# Revit family: D9515-DN25-RFA_2018
name_source: partatom
category: Pipe Accessories
revit_build: Autodesk Revit LT 2018 (Build: 20180329_1100(x64)
units: mm (PartAtom-declared; Revit-internal decimal feet)

## family parameters
Always vertical = Yes
Cut with Voids When Loaded = No
Part Type = Valve - Breaks Into
Round Connector Dimension = Use Diameter
Shared = No
Work Plane-Based = No

## types (6) — shared parameters
CAT0 = Yes
Description = Ruční vyvažovací ventil s měřením na cloně; PN25
H11 = 32 mm  [stored 0.104987 ft]
H13 = 9 mm  [stored 0.0295276 ft]
H15 = 20 mm  [stored 0.0656168 ft]
HWR = 35 mm  [stored 0.114829 ft]
L21 = 8 mm  [stored 0.0262467 ft]
L22 = 21 mm  [stored 0.0688976 ft]
L2D = 88 mm
L2D_Min = 3048 mm
L4 = 21 mm  [stored 0.0688976 ft]
L4__ve = -21 mm  [stored -0.0688976 ft]
L5 = 2 mm  [stored 0.00656168 ft]
Manufacturer = Hydronix
NUT1 = No
QmdConnectorList = 301;D;302;D
R14 = 20 mm  [stored 0.0656168 ft]
R6 = 8 mm  [stored 0.0262467 ft]
R7 = 9 mm  [stored 0.0295276 ft]
Type Comments = Ruční vyvažovací ventil s měřením na cloně; PN25; -10~+130°C; (měřicí vsuvky -10~+120°C)
URL = www.hydronix.cz
W2D = 15 mm  [stored 0.0492126 ft]
magiPartTypeId = 304
magiProductFamilyId = 2231140663314cd0b01ba8939d6b11

## per-type parameters (varying)
- D9515 DN15: CenSd_RN2_6=15 mm  [stored 0.0492126 ft]; CenSd_RN_6=15 mm  [stored 0.0492126 ft]; D=15 mm; H10=4 mm  [stored 0.0131234 ft]; H12=10 mm  [stored 0.0328084 ft]; H14=19 mm; H21=7 mm  [stored 0.0229659 ft]; H22=7 mm  [stored 0.0229659 ft]; H23=12 mm  [stored 0.0393701 ft]; H24=31 mm; L1=8 mm  [stored 0.0262467 ft]; L1__ve=-8 mm  [stored -0.0262467 ft]; L2=12 mm  [stored 0.0393701 ft]; L2__ve=-12 mm  [stored -0.0393701 ft]; L3=10 mm  [stored 0.0328084 ft]; L_2=44 mm; MC Product Code=9515 015 (DN15, PN25; kvs1,92; kvc2,80); R1=11 mm; R11=15 mm  [stored 0.0492126 ft]; R12=16 mm  [stored 0.0524934 ft]; R13=15 mm  [stored 0.0492126 ft]; R2=14 mm  [stored 0.0459318 ft]; R3=15 mm  [stored 0.0492126 ft]; RN=18 mm  [stored 0.0590551 ft]; RN2=18 mm  [stored 0.0590551 ft]; W21=7 mm  [stored 0.0229659 ft]; magiProductId=17cbc467cde14417a5a74aa240a316
- D9515 DN20: CenSd_RN2_6=17 mm  [stored 0.0557743 ft]; CenSd_RN_6=17 mm  [stored 0.0557743 ft]; D=20 mm; H10=5 mm  [stored 0.0164042 ft]; H12=10 mm  [stored 0.0328084 ft]; H14=18 mm  [stored 0.0590551 ft]; H21=8 mm  [stored 0.0262467 ft]; H22=8 mm  [stored 0.0262467 ft]; H23=12 mm  [stored 0.0393701 ft]; H24=31 mm; L1=9 mm  [stored 0.0295276 ft]; L1__ve=-9 mm  [stored -0.0295276 ft]; L2=12 mm  [stored 0.0393701 ft]; L2__ve=-12 mm  [stored -0.0393701 ft]; L3=10 mm  [stored 0.0328084 ft]; L_2=48 mm; MC Product Code=9515 020 (DN20, PN25; kvs3,67; kvc5,33); R1=13 mm  [stored 0.0426509 ft]; R11=16 mm  [stored 0.0524934 ft]; R12=18 mm  [stored 0.0590551 ft]; R13=16 mm  [stored 0.0524934 ft]; R2=15 mm  [stored 0.0492126 ft]; R3=16 mm  [stored 0.0524934 ft]; RN=20 mm  [stored 0.0656168 ft]; RN2=20 mm  [stored 0.0656168 ft]; W21=8 mm  [stored 0.0262467 ft]; magiProductId=db511cd39f454f418d6e49e6ac0c56
- D9515 DN25: CenSd_RN2_6=19 mm; CenSd_RN_6=19 mm; D=25 mm; H10=6 mm  [stored 0.019685 ft]; H12=10 mm  [stored 0.0328084 ft]; H14=17 mm  [stored 0.0557743 ft]; H21=10 mm  [stored 0.0328084 ft]; H22=10 mm  [stored 0.0328084 ft]; H23=12 mm  [stored 0.0393701 ft]; H24=31 mm; L1=10 mm  [stored 0.0328084 ft]; L1__ve=-10 mm  [stored -0.0328084 ft]; L2=14 mm  [stored 0.0459318 ft]; L2__ve=-14 mm  [stored -0.0459318 ft]; L3=12 mm  [stored 0.0393701 ft]; L_2=50 mm; MC Product Code=9515 025 (DN25, PN25; kvs6,24; kvc9,72); R1=14 mm  [stored 0.0459318 ft]; R11=18 mm  [stored 0.0590551 ft]; R12=20 mm  [stored 0.0656168 ft]; R13=18 mm  [stored 0.0590551 ft]; R2=17 mm  [stored 0.0557743 ft]; R3=18 mm  [stored 0.0590551 ft]; RN=21 mm  [stored 0.0688976 ft]; RN2=21 mm  [stored 0.0688976 ft]; W21=8 mm  [stored 0.0262467 ft]; magiProductId=e8aaae3d88cc438088acb51c2ae749
- D9515 DN32: CenSd_RN2_6=18 mm  [stored 0.0590551 ft]; CenSd_RN_6=21 mm  [stored 0.0688976 ft]; D=32 mm; H10=7 mm  [stored 0.0229659 ft]; H12=15 mm  [stored 0.0492126 ft]; H14=37 mm; H21=12 mm  [stored 0.0393701 ft]; H22=12 mm  [stored 0.0393701 ft]; H23=15 mm  [stored 0.0492126 ft]; H24=37 mm; L1=11 mm; L1__ve=-11 mm; L2=15 mm  [stored 0.0492126 ft]; L2__ve=-15 mm  [stored -0.0492126 ft]; L3=13 mm  [stored 0.0426509 ft]; L_2=59 mm; MC Product Code=9515 032 (DN32, PN25; kvs12,54; kvc20,25); R1=16 mm  [stored 0.0524934 ft]; R11=20 mm  [stored 0.0656168 ft]; R12=22 mm; R13=17 mm  [stored 0.0557743 ft]; R2=19 mm; R3=20 mm  [stored 0.0656168 ft]; RN=24 mm  [stored 0.0787402 ft]; RN2=20 mm  [stored 0.0656168 ft]; W21=9 mm  [stored 0.0295276 ft]; magiProductId=dc2d0354abae4200a8eaff76faf524
- D9515 DN40: CenSd_RN2_6=18 mm  [stored 0.0590551 ft]; CenSd_RN_6=24 mm  [stored 0.0787402 ft]; D=40 mm; H10=8 mm  [stored 0.0262467 ft]; H12=15 mm  [stored 0.0492126 ft]; H14=39 mm; H21=15 mm  [stored 0.0492126 ft]; H22=15 mm  [stored 0.0492126 ft]; H23=15 mm  [stored 0.0492126 ft]; H24=38 mm; L1=13 mm  [stored 0.0426509 ft]; L1__ve=-13 mm  [stored -0.0426509 ft]; L2=16 mm  [stored 0.0524934 ft]; L2__ve=-16 mm  [stored -0.0524934 ft]; L3=14 mm  [stored 0.0459318 ft]; L_2=64 mm; MC Product Code=9515 040 (DN40, PN25; kvs19,59; kvc30,23); R1=18 mm  [stored 0.0590551 ft]; R11=23 mm; R12=25 mm  [stored 0.082021 ft]; R13=17 mm  [stored 0.0557743 ft]; R2=21 mm  [stored 0.0688976 ft]; R3=23 mm; RN=27 mm; RN2=20 mm  [stored 0.0656168 ft]; W21=11 mm; magiProductId=9b6b6dd7761a428fa780a8a57ab3c3
- D9515 DN50: CenSd_RN2_6=18 mm  [stored 0.0590551 ft]; CenSd_RN_6=27 mm; D=50 mm; H10=10 mm  [stored 0.0328084 ft]; H12=15 mm  [stored 0.0492126 ft]; H14=51 mm; H21=18 mm  [stored 0.0590551 ft]; H22=18 mm  [stored 0.0590551 ft]; H23=16 mm  [stored 0.0524934 ft]; H24=41 mm; L1=15 mm  [stored 0.0492126 ft]; L1__ve=-15 mm  [stored -0.0492126 ft]; L2=17 mm  [stored 0.0557743 ft]; L2__ve=-17 mm  [stored -0.0557743 ft]; L3=15 mm  [stored 0.0492126 ft]; L_2=73 mm; MC Product Code=9515 050 (DN50, PN25; kvs29,72; kvc55,07); R1=20 mm  [stored 0.0656168 ft]; R11=26 mm  [stored 0.0853018 ft]; R12=29 mm; R13=17 mm  [stored 0.0557743 ft]; R2=24 mm  [stored 0.0787402 ft]; R3=26 mm  [stored 0.0853018 ft]; RN=31 mm; RN2=20 mm  [stored 0.0656168 ft]; W21=12 mm  [stored 0.0393701 ft]; magiProductId=6b5b9dd02a164b53a7f96efb176f34

note: [stored X ft] marks values corroborated as IEEE doubles in the binary element streams (Revit-internal decimal feet)

## geometry (parser evidence)
native form markers: Sweep x1
no freeform markers — native parametric forms only
